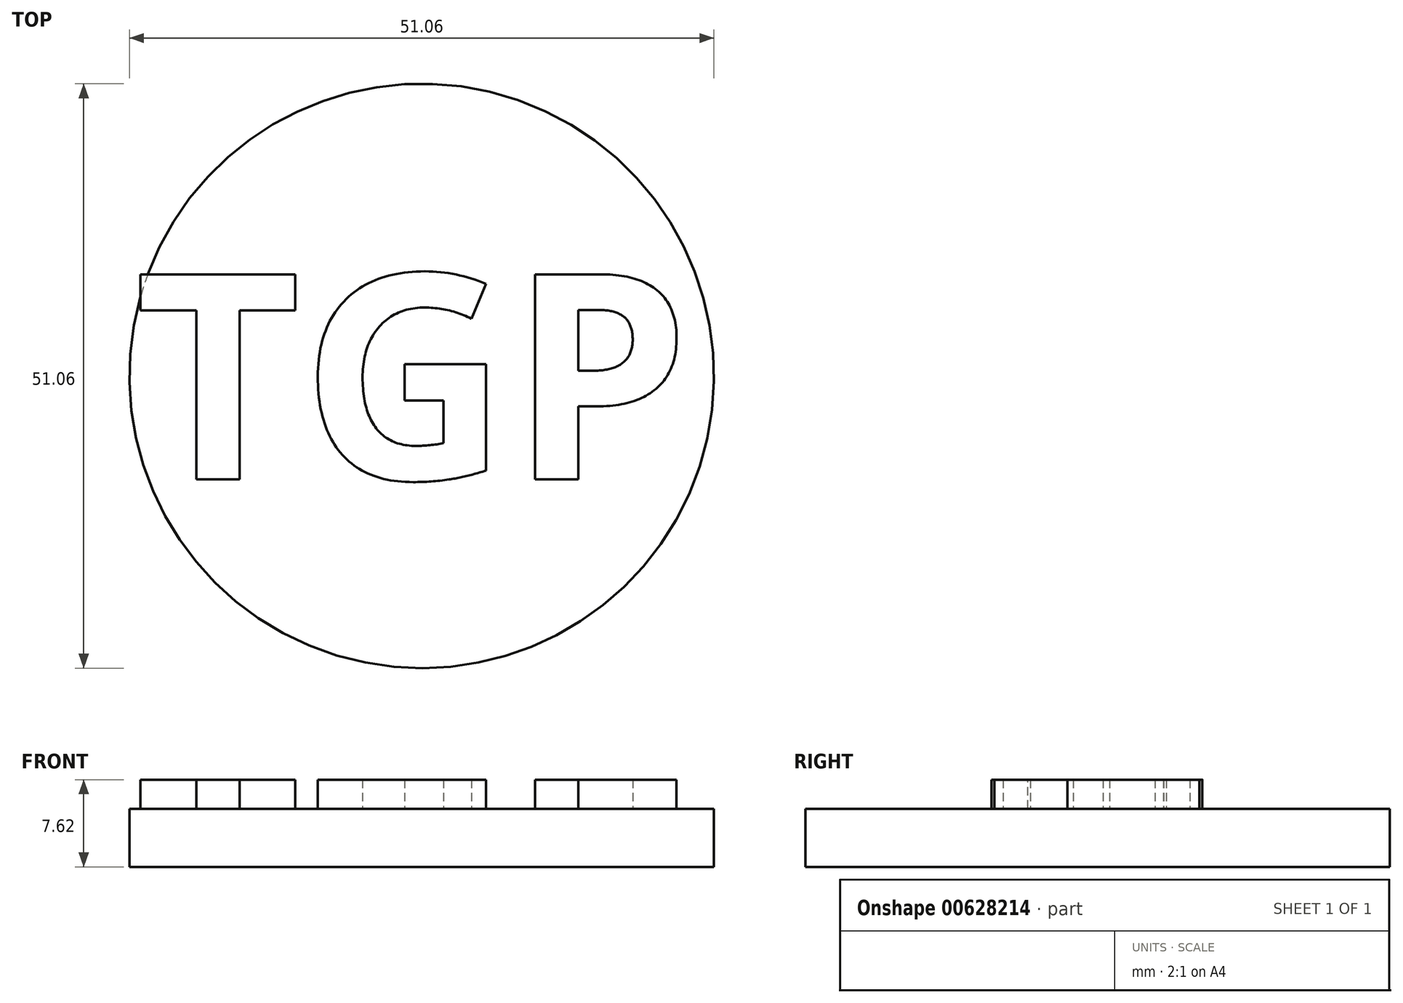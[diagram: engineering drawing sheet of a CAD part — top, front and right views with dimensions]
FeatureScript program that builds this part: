
annotation { "Feature Type Name" : "Feature", "Feature Type Description" : "" }
export const myFeature = defineFeature(function(context is Context, id is Id, definition is map)
    precondition{}
    {
        {
            var Q0;
            Q0=qCreatedBy(makeId("Top.planeOp"),FACE);
            var sketch = newSketch(context, id + "F0", { "sketchPlane" : qUnion([Q0])});
            skCircle(sketch, "E0", {"center": v(0, 0) * mm, "radius": 25.53 * mm});
            skSolve(sketch);
        }
        {
            var Q0;
            Q0=makeQuery(id+"F0.imprint","IMPRINT",FACE,{"disambiguationData":[TD([[makeQuery(id+"F0.imprint","IMPRINT",EDGE,{"derivedFrom":sQuery(id+"F0.wireOp",EDGE,"E0")}),1.0]])]});
            extrude(context, id + "F1", {"entities" : qUnion([Q0]), "depth" : 5.08 * mm, "offsetDistance" : 25.4 * mm});
        }
        {
            var Q0;
            Q0=makeQuery(id+"F1.opExtrude","CAP_FACE",FACE,{"disambiguationData":[OSD([sQuery(id+"F0.wireOp",EDGE,"E0")])],"isStart":false});
            var sketch = newSketch(context, id + "F2", { "sketchPlane" : qUnion([Q0])});
            skText(sketch, "E1", { "text": "TGP", "fontName": "OpenSans-Bold.ttf"});
            const initialGuessF2  = {"E1": [-0.02507, -0.00903, 1, 0, 0.01807]};
            skSetInitialGuess(sketch, initialGuessF2);
            skSolve(sketch);
        }
        {
            var Q0;
            Q0 = qSketchRegion(id + "F2", true);
            extrude(context, id + "F3", {"entities" : qUnion([Q0]), "operationType" : NewBodyOperationType.ADD, "depth" : 2.54 * mm, "offsetDistance" : 25.4 * mm});
        }
    });
